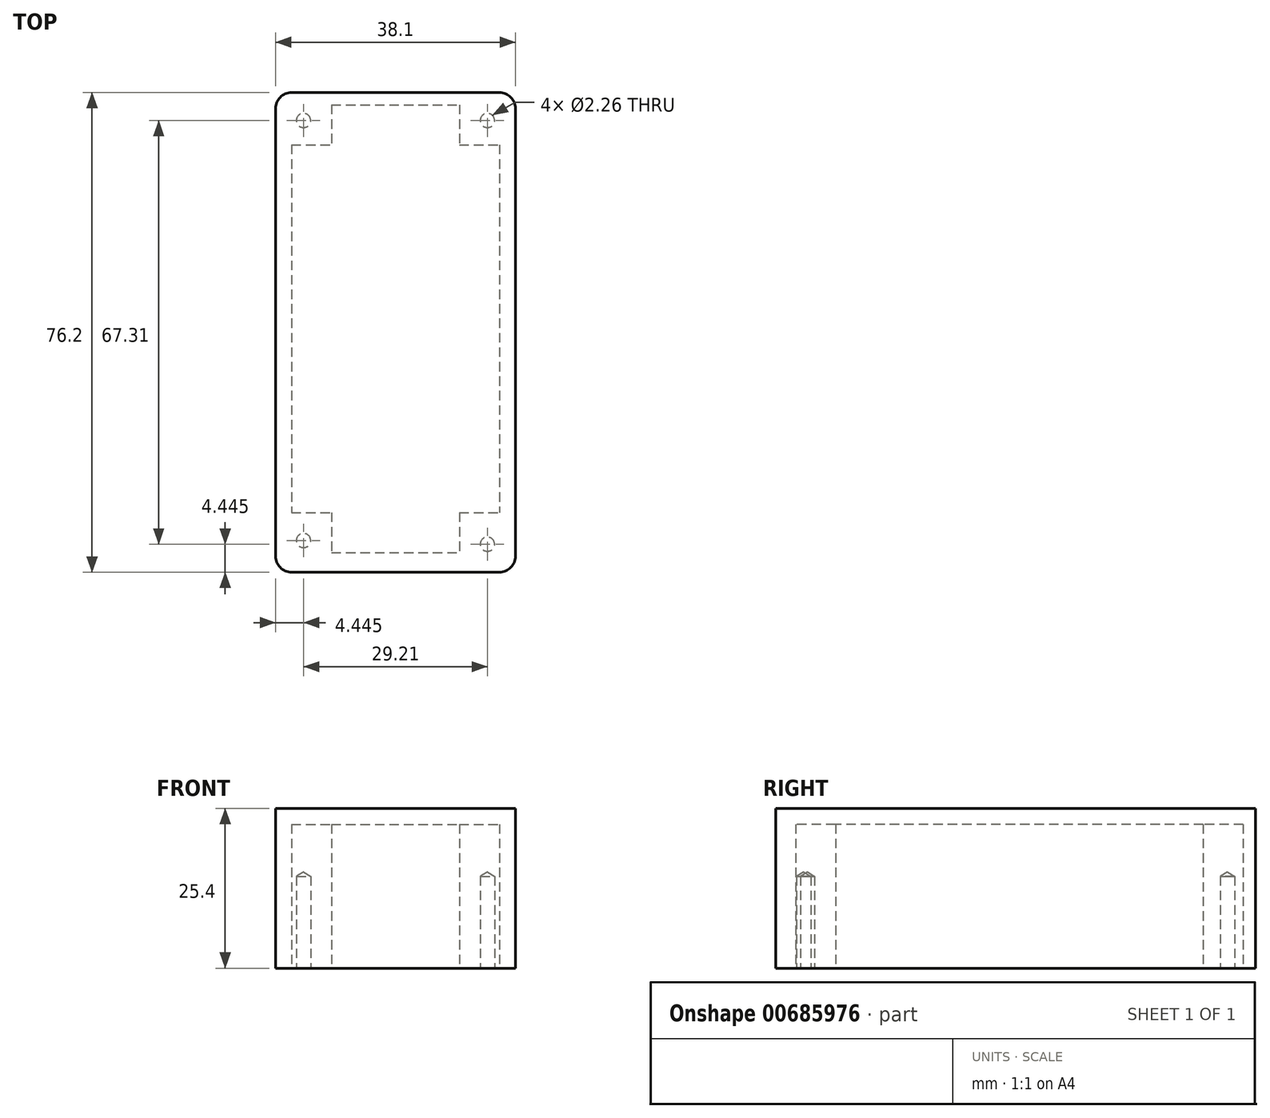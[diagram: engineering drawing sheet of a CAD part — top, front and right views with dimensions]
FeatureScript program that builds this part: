
annotation { "Feature Type Name" : "Feature", "Feature Type Description" : "" }
export const myFeature = defineFeature(function(context is Context, id is Id, definition is map)
    precondition{}
    {
        {
            var Q0;
            Q0=qCreatedBy(makeId("Top.planeOp"),FACE);
            var sketch = newSketch(context, id + "F0", { "sketchPlane" : qUnion([Q0])});
            skLineSegment(sketch, "E0.bottom", {"start": v(-19.05, -38.1) * mm, "end": v(19.05, -38.1) * mm});
            skLineSegment(sketch, "E0.top", {"start": v(-19.05, 38.1) * mm, "end": v(19.05, 38.1) * mm});
            skLineSegment(sketch, "E0.left", {"start": v(-19.05, -38.1) * mm, "end": v(-19.05, 38.1) * mm});
            skLineSegment(sketch, "E0.right", {"start": v(19.05, -38.1) * mm, "end": v(19.05, 38.1) * mm});
            skPoint(sketch, "E0.middle", {"position": v(0, 0) * mm});
            skSolve(sketch);
        }
        {
            var Q0;
            Q0=makeQuery(id+"F0.imprint","IMPRINT",FACE,{"disambiguationData":[TD([[makeQuery(id+"F0.imprint","IMPRINT",EDGE,{"derivedFrom":sQuery(id+"F0.wireOp",EDGE,"E0.bottom")}),1.0]])]});
            extrude(context, id + "F1", {"entities" : qUnion([Q0]), "depth" : 25.4 * mm, "offsetDistance" : 25.4 * mm});
        }
        {
            var Q0;
            Q0=qCreatedBy(makeId("Top.planeOp"),FACE);
            var sketch = newSketch(context, id + "F2", { "sketchPlane" : qUnion([Q0])});
            skLineSegment(sketch, "E1.bottom", {"start": v(-10.16, 36.15) * mm, "end": v(10.16, 36.15) * mm});
            skLineSegment(sketch, "E1.top", {"start": v(-10.16, -34.97) * mm, "end": v(10.16, -34.97) * mm});
            skLineSegment(sketch, "E1.left", {"start": v(-16.5, 29.8) * mm, "end": v(-16.5, -28.62) * mm});
            skLineSegment(sketch, "E1.right", {"start": v(16.51, 29.8) * mm, "end": v(16.51, -28.62) * mm});
            skPoint(sketch, "E1.middle", {"position": v(0, 0) * mm});
            skLineSegment(sketch, "E2.top", {"start": v(-16.5, 29.8) * mm, "end": v(-10.16, 29.8) * mm});
            skLineSegment(sketch, "E2.right", {"start": v(-10.16, 36.15) * mm, "end": v(-10.16, 29.8) * mm});
            skLineSegment(sketch, "E3.top", {"start": v(10.16, 29.8) * mm, "end": v(16.51, 29.8) * mm});
            skLineSegment(sketch, "E3.left", {"start": v(10.16, 36.15) * mm, "end": v(10.16, 29.8) * mm});
            skLineSegment(sketch, "E4.bottom", {"start": v(-16.5, -28.62) * mm, "end": v(-10.16, -28.62) * mm});
            skLineSegment(sketch, "E4.right", {"start": v(-10.16, -28.62) * mm, "end": v(-10.16, -34.97) * mm});
            skLineSegment(sketch, "E5.bottom", {"start": v(10.16, -28.62) * mm, "end": v(16.51, -28.62) * mm});
            skLineSegment(sketch, "E5.left", {"start": v(10.16, -28.62) * mm, "end": v(10.16, -34.97) * mm});
            skPoint(sketch, "E6", {"position": v(-14.6, 33.66) * mm});
            skPoint(sketch, "E7", {"position": v(14.6, 33.66) * mm});
            skPoint(sketch, "E8", {"position": v(-14.6, -33.06) * mm});
            skPoint(sketch, "E9", {"position": v(14.6, -33.66) * mm});
            skSolve(sketch);
        }
        {
            var Q0;
            Q0 = qSketchRegion(id + "F2", true);
            extrude(context, id + "F3", {"entities" : qUnion([Q0]), "operationType" : NewBodyOperationType.REMOVE, "depth" : 22.86 * mm, "offsetDistance" : 25.4 * mm});
        }
        {
            var Q0;
            Q0=sQuery(id+"F2.wireOp",VERTEX,"E6");
            var Q1;
            Q1=sQuery(id+"F2.wireOp",VERTEX,"E7");
            var Q2;
            Q2=sQuery(id+"F2.wireOp",VERTEX,"E9");
            var Q3;
            Q3=sQuery(id+"F2.wireOp",VERTEX,"E8");
            var Q4;
            Q4=makeQuery(id+"F1.opExtrude","SWEPT_BODY",BODY,{"disambiguationData":[OSD([sQuery(id+"F0.wireOp",EDGE,"E0.bottom"),sQuery(id+"F0.wireOp",EDGE,"E0.top"),sQuery(id+"F0.wireOp",EDGE,"E0.left"),sQuery(id+"F0.wireOp",EDGE,"E0.right")])]});
            hole(context, id + "F4", {"style" : HoleStyle.SIMPLE, "endStyle" : HoleEndStyle.BLIND, "oppositeDirection" : true, "standardTappedOrClearance" : lookupTablePath({ "standard" : "ANSI", "engagement" : "75%", "pitch" : "40 tpi", "size" : "#4", "type" : "Tapped" }), "standardBlindInLast" : lookupTablePath({ "standard" : "ANSI", "fit" : "Normal", "engagement" : "75%", "pitch" : "40 tpi", "size" : "#4", "type" : "Clearance & tapped" }), "holeDiameter" : 2.26 * mm, "majorDiameter" : 2.84 * mm, "showTappedDepth" : true, "holeDepth" : 14.6 * mm, "isTappedThrough" : true, "tappedDepth" : 12.7 * mm, "tapClearance" : 3, "locations" : qUnion([Q0, Q1, Q2, Q3]), "scope" : qUnion([Q4])});
        }
        {
            var Q0;
            Q0=makeQuery(id+"F1.opExtrude","SWEPT_EDGE",EDGE,{"disambiguationData":[OSD([sQuery(id+"F0.wireOp",EDGE,"E0.bottom"),sQuery(id+"F0.wireOp",EDGE,"E0.right")])]});
            var Q1;
            Q1=makeQuery(id+"F1.opExtrude","SWEPT_EDGE",EDGE,{"disambiguationData":[OSD([sQuery(id+"F0.wireOp",EDGE,"E0.bottom"),sQuery(id+"F0.wireOp",EDGE,"E0.left")])]});
            var Q2;
            Q2=makeQuery(id+"F1.opExtrude","SWEPT_EDGE",EDGE,{"disambiguationData":[OSD([sQuery(id+"F0.wireOp",EDGE,"E0.top"),sQuery(id+"F0.wireOp",EDGE,"E0.left")])]});
            var Q3;
            Q3=makeQuery(id+"F1.opExtrude","SWEPT_EDGE",EDGE,{"disambiguationData":[OSD([sQuery(id+"F0.wireOp",EDGE,"E0.top"),sQuery(id+"F0.wireOp",EDGE,"E0.right")])]});
            fillet(context, id + "F5", {"entities" : qUnion([Q0, Q1, Q2, Q3]), "radius" : 2.54 * mm, "tangentPropagation" : true, "allowEdgeOverflow" : false});
        }
    });
